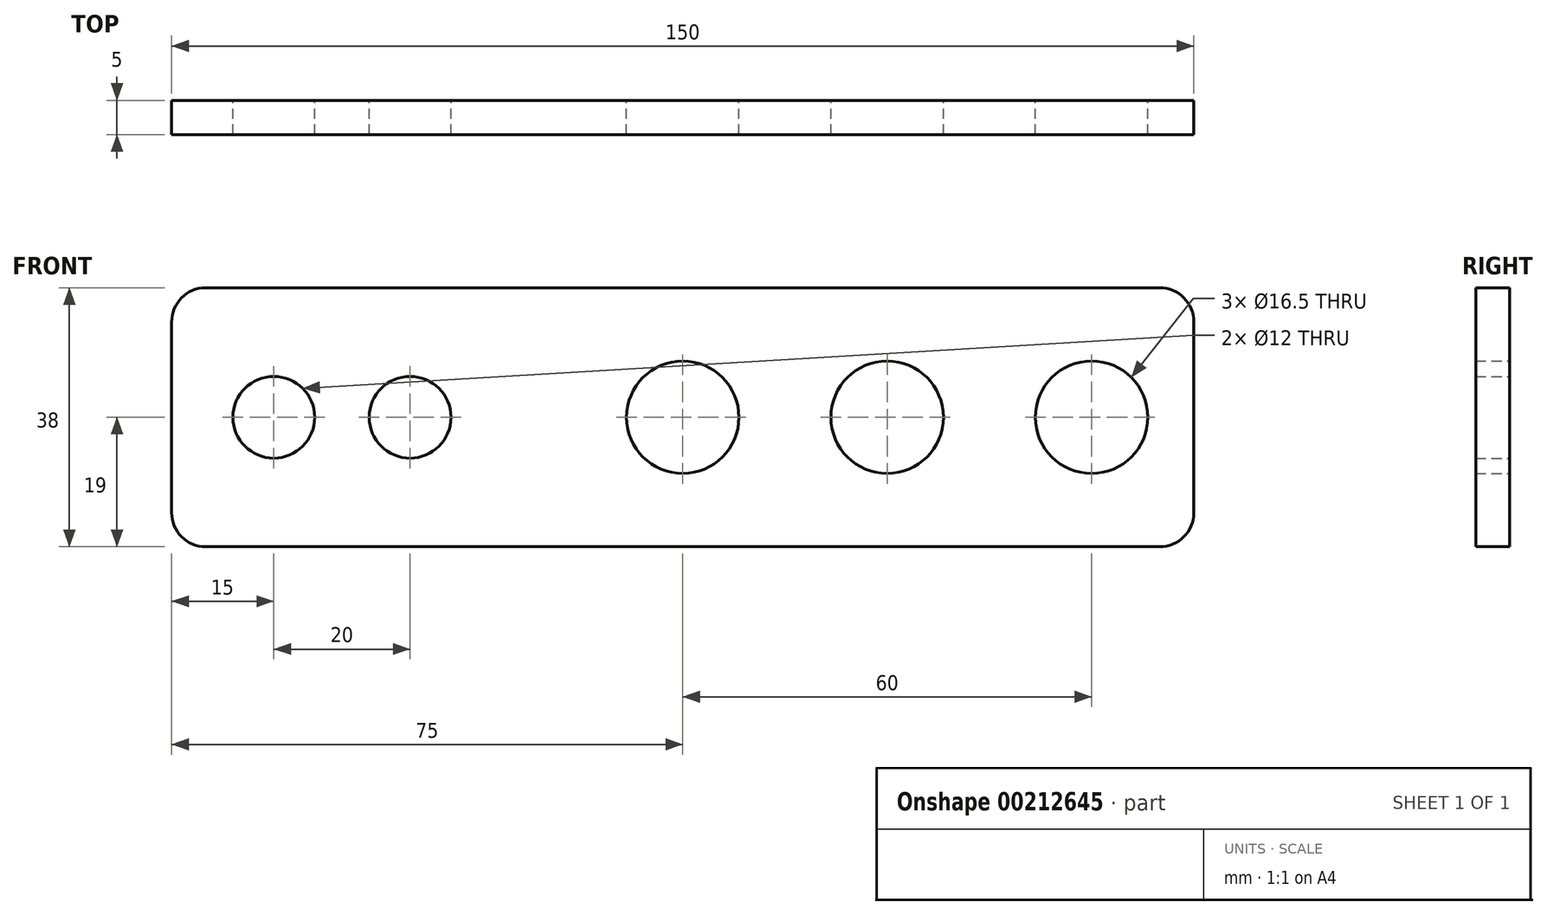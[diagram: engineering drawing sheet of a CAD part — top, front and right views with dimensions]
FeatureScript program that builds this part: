
annotation { "Feature Type Name" : "Feature", "Feature Type Description" : "" }
export const myFeature = defineFeature(function(context is Context, id is Id, definition is map)
    precondition{}
    {
        {
            var Q0;
            Q0=qCreatedBy(makeId("Front.planeOp"),FACE);
            var sketch = newSketch(context, id + "F0", { "sketchPlane" : qUnion([Q0])});
            skLineSegment(sketch, "E0.bottom", {"start": v(-75, 19) * mm, "end": v(75, 19) * mm});
            skLineSegment(sketch, "E0.top", {"start": v(-75, -19) * mm, "end": v(75, -19) * mm});
            skLineSegment(sketch, "E0.left", {"start": v(-75, 19) * mm, "end": v(-75, -19) * mm});
            skLineSegment(sketch, "E0.right", {"start": v(75, 19) * mm, "end": v(75, -19) * mm});
            skCircle(sketch, "E1", {"center": v(0, 0) * mm, "radius": 8.25 * mm});
            skCircle(sketch, "E2", {"center": v(30, 0) * mm, "radius": 8.25 * mm});
            skCircle(sketch, "E3", {"center": v(60, 0) * mm, "radius": 8.25 * mm});
            skCircle(sketch, "E4", {"center": v(-40, 0) * mm, "radius": 6 * mm});
            skCircle(sketch, "E5", {"center": v(-60, 0) * mm, "radius": 6 * mm});
            skSolve(sketch);
        }
        {
            var Q0;
            Q0 = qSketchRegion(id + "F0", true);
            extrude(context, id + "F1", {"entities" : qUnion([Q0]), "depth" : 5 * mm});
        }
        {
            var Q0;
            Q0=makeQuery(id+"F1.opExtrude","SWEPT_EDGE",EDGE,{"disambiguationData":[OSD([sQuery(id+"F0.wireOp",EDGE,"E0.bottom"),sQuery(id+"F0.wireOp",EDGE,"E0.left")])]});
            var Q1;
            Q1=makeQuery(id+"F1.opExtrude","SWEPT_EDGE",EDGE,{"disambiguationData":[OSD([sQuery(id+"F0.wireOp",EDGE,"E0.top"),sQuery(id+"F0.wireOp",EDGE,"E0.left")])]});
            var Q2;
            Q2=makeQuery(id+"F1.opExtrude","SWEPT_EDGE",EDGE,{"disambiguationData":[OSD([sQuery(id+"F0.wireOp",EDGE,"E0.bottom"),sQuery(id+"F0.wireOp",EDGE,"E0.right")])]});
            var Q3;
            Q3=makeQuery(id+"F1.opExtrude","SWEPT_EDGE",EDGE,{"disambiguationData":[OSD([sQuery(id+"F0.wireOp",EDGE,"E0.top"),sQuery(id+"F0.wireOp",EDGE,"E0.right")])]});
            fillet(context, id + "F2", {"entities" : qUnion([Q0, Q1, Q2, Q3]), "radius" : 5 * mm, "tangentPropagation" : true, "allowEdgeOverflow" : false});
        }
    });
